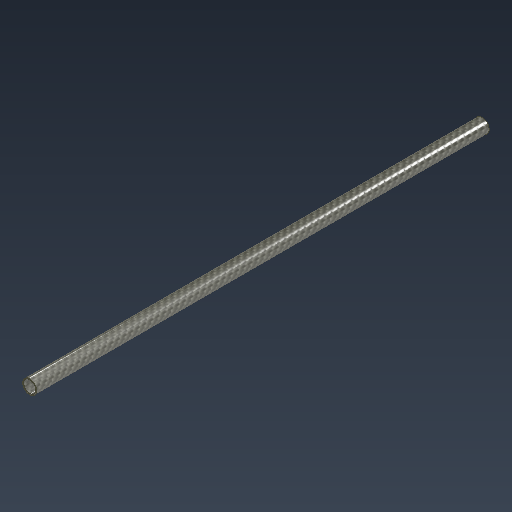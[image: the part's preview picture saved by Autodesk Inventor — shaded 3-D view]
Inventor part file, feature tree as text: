
AUTODESK INVENTOR PART (.ipt)
format: ipt  version: 2024.1 (Build 281209000, 209)  size: 118,272 bytes
history: native  units: mm
features: extrude x1
ambient origin geometry x8: Origin, YZ Plane, XZ Plane, XY Plane, X Axis, Y Axis, Z Axis, Center Point
bodies: Solid1 (feature_tree)
feature tree (1):
  extrude  "Extrusion1"  Depth=16.0mm
